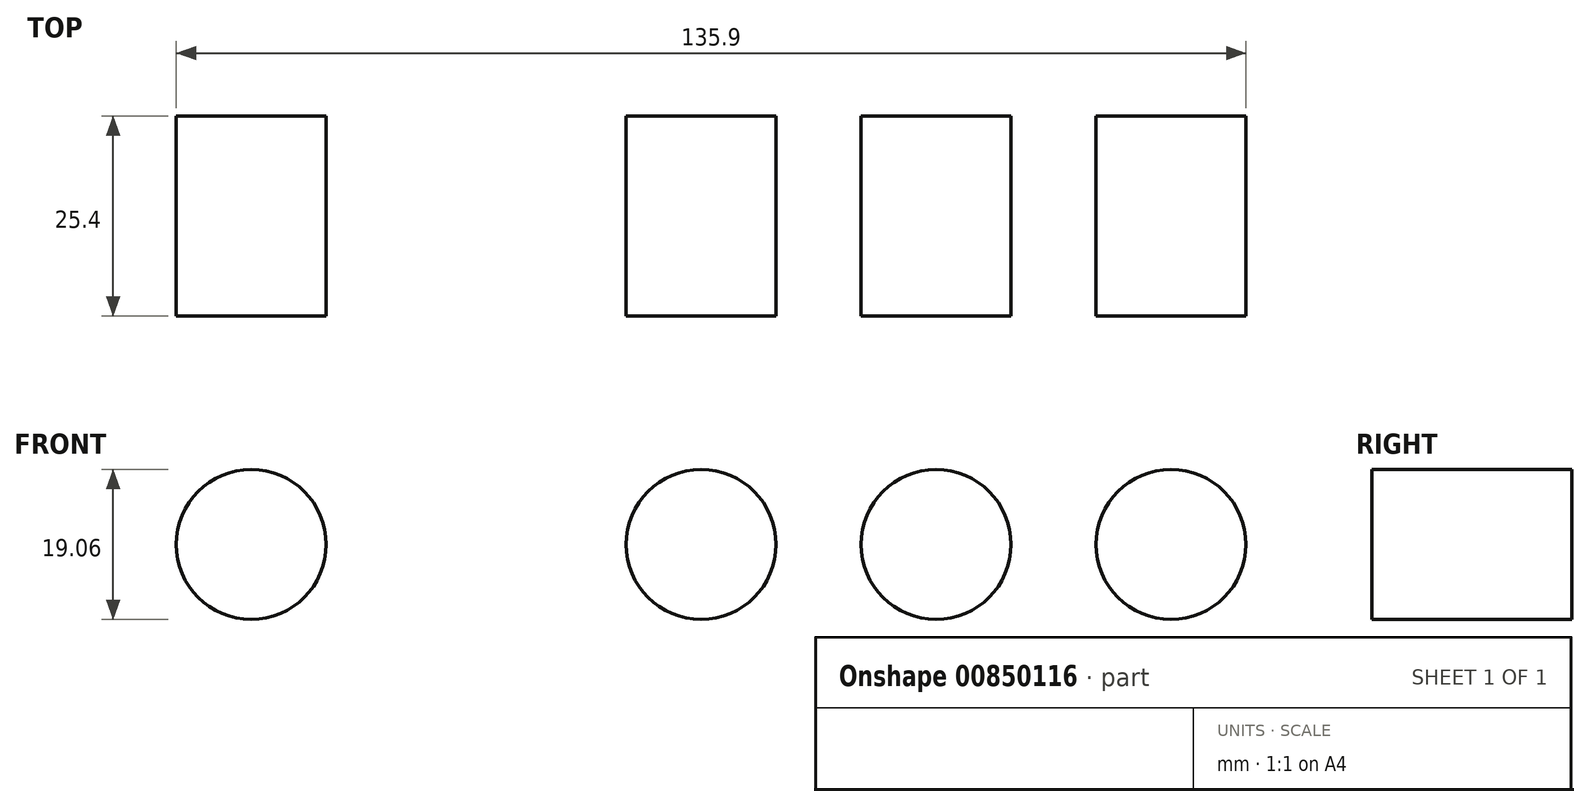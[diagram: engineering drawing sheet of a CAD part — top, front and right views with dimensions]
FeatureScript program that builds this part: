
annotation { "Feature Type Name" : "Feature", "Feature Type Description" : "" }
export const myFeature = defineFeature(function(context is Context, id is Id, definition is map)
    precondition{}
    {
        {
            var Q0;
            Q0=qCreatedBy(makeId("Front.planeOp"),FACE);
            var sketch = newSketch(context, id + "F0", { "sketchPlane" : qUnion([Q0])});
            skCircle(sketch, "E0", {"center": v(0, 0) * mm, "radius": 9.53 * mm});
            skCircle(sketch, "E1.1.0.0", {"center": v(57.15, 0) * mm, "radius": 9.53 * mm});
            skCircle(sketch, "E1.2.0.0", {"center": v(87, 0) * mm, "radius": 9.53 * mm});
            skCircle(sketch, "E1.3.0.0", {"center": v(116.84, 0) * mm, "radius": 9.53 * mm});
            skLineSegment(sketch, "E2", {"start": v(0, 39.47) * mm, "end": v(0, -45.33) * mm, "construction": true});
            skLineSegment(sketch, "E3", {"start": v(116.84, 43.8) * mm, "end": v(116.84, -47.22) * mm, "construction": true});
            skSolve(sketch);
        }
        {
            var Q0;
            Q0=makeQuery(id+"F0.imprint","IMPRINT",FACE,{"disambiguationData":[TD([[makeQuery(id+"F0.imprint","IMPRINT",EDGE,{"derivedFrom":sQuery(id+"F0.wireOp",EDGE,"E1.2.0.0")}),1.0]])]});
            var Q1;
            Q1=makeQuery(id+"F0.imprint","IMPRINT",FACE,{"disambiguationData":[TD([[makeQuery(id+"F0.imprint","IMPRINT",EDGE,{"derivedFrom":sQuery(id+"F0.wireOp",EDGE,"E1.3.0.0")}),1.0]])]});
            var Q2;
            Q2=makeQuery(id+"F0.imprint","IMPRINT",FACE,{"disambiguationData":[TD([[makeQuery(id+"F0.imprint","IMPRINT",EDGE,{"derivedFrom":sQuery(id+"F0.wireOp",EDGE,"E1.1.0.0")}),1.0]])]});
            var Q3;
            Q3=makeQuery(id+"F0.imprint","IMPRINT",FACE,{"disambiguationData":[TD([[makeQuery(id+"F0.imprint","IMPRINT",EDGE,{"derivedFrom":sQuery(id+"F0.wireOp",EDGE,"E0")}),1.0]])]});
            extrude(context, id + "F1", {"entities" : qUnion([Q0, Q1, Q2, Q3]), "depth" : 25.4 * mm, "offsetDistance" : 25.4 * mm});
        }
    });
